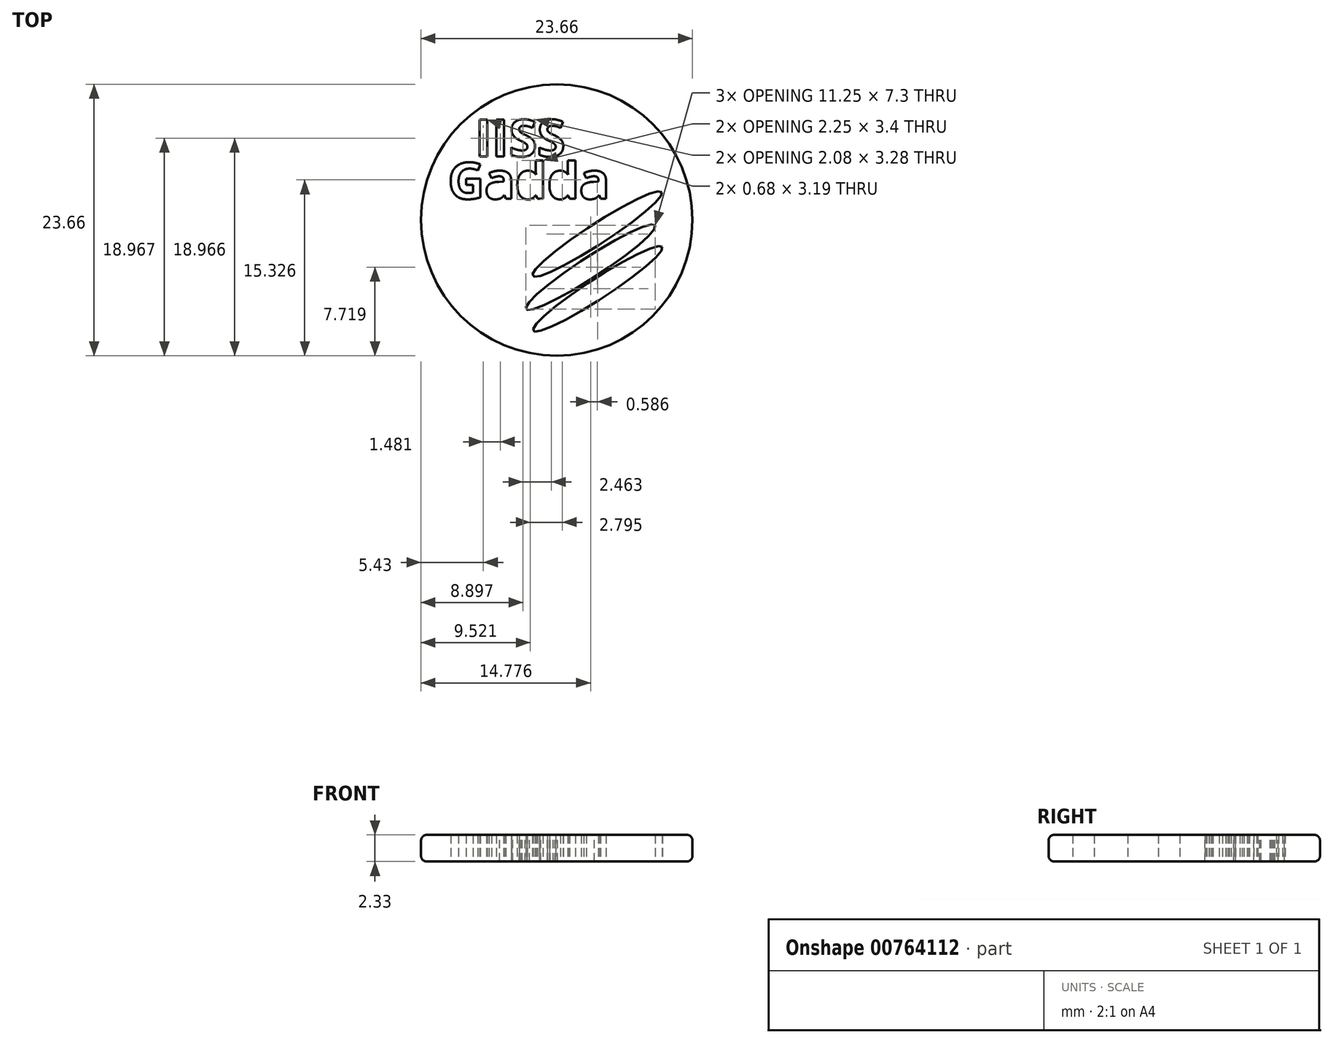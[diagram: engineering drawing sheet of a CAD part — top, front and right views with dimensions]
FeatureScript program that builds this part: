
annotation { "Feature Type Name" : "Feature", "Feature Type Description" : "" }
export const myFeature = defineFeature(function(context is Context, id is Id, definition is map)
    precondition{}
    {
        {
            assignVariable(context, id + "F0", {"name" : "SPESS", "anyValue" : 2.33});
        }
        {
            var Q0;
            Q0=qCreatedBy(makeId("Top.planeOp"),FACE);
            var sketch = newSketch(context, id + "F1", { "sketchPlane" : qUnion([Q0])});
            skCircle(sketch, "E0", {"center": v(0, 0) * mm, "radius": 11.82 * mm});
            skEllipse(sketch, "E1", {"center": v(3.53, -1.22) * mm, "majorRadius": 6.7 * mm, "minorRadius": 0.9 * mm, "majorAxis": v(0.84, 0.54)});
            skEllipse(sketch, "E2", {"center": v(2.95, -4.11) * mm, "majorRadius": 6.7 * mm, "minorRadius": 0.9 * mm, "majorAxis": v(0.84, 0.54)});
            skEllipse(sketch, "E3", {"center": v(3.58, -6) * mm, "majorRadius": 6.7 * mm, "minorRadius": 0.9 * mm, "majorAxis": v(0.84, 0.54)});
            skText(sketch, "E4", { "text": "IISS", "fontName": "OpenSans-Bold.ttf"});
            skText(sketch, "E5", { "text": "Gadda", "fontName": "OpenSans-Bold.ttf"});
            const initialGuessF1  = {"E4": [-0.00714, 0.00554, 1, 0, 0.00322], "E5": [-0.0095, 0.00184, 1, 0, 0.00318]};
            skSetInitialGuess(sketch, initialGuessF1);
            skSolve(sketch);
        }
        {
            var Q0;
            Q0=makeQuery(id+"F1.imprint","IMPRINT",FACE,{"disambiguationData":[TD([[makeQuery(id+"F1.imprint","IMPRINT",EDGE,{"derivedFrom":sQuery(id+"F1.wireOp",EDGE,"E0")}),1.0]])]});
            extrude(context, id + "F2", {"entities" : qUnion([Q0]), "depth" : (getVariable(context, 'SPESS')) * mm, "offsetDistance" : 25 * mm});
        }
        {
            var Q0;
            Q0=makeQuery(id+"F2.opExtrude","CAP_EDGE",EDGE,{"disambiguationData":[OSD([sQuery(id+"F1.wireOp",EDGE,"E0")])],"isStart":false});
            var Q1;
            Q1=makeQuery(id+"F2.opExtrude","CAP_EDGE",EDGE,{"disambiguationData":[OSD([sQuery(id+"F1.wireOp",EDGE,"E0")])],"isStart":true});
            fillet(context, id + "F3", {"entities" : qUnion([Q0, Q1]), "radius" : .5 * mm, "tangentPropagation" : true, "allowEdgeOverflow" : false});
        }
    });
